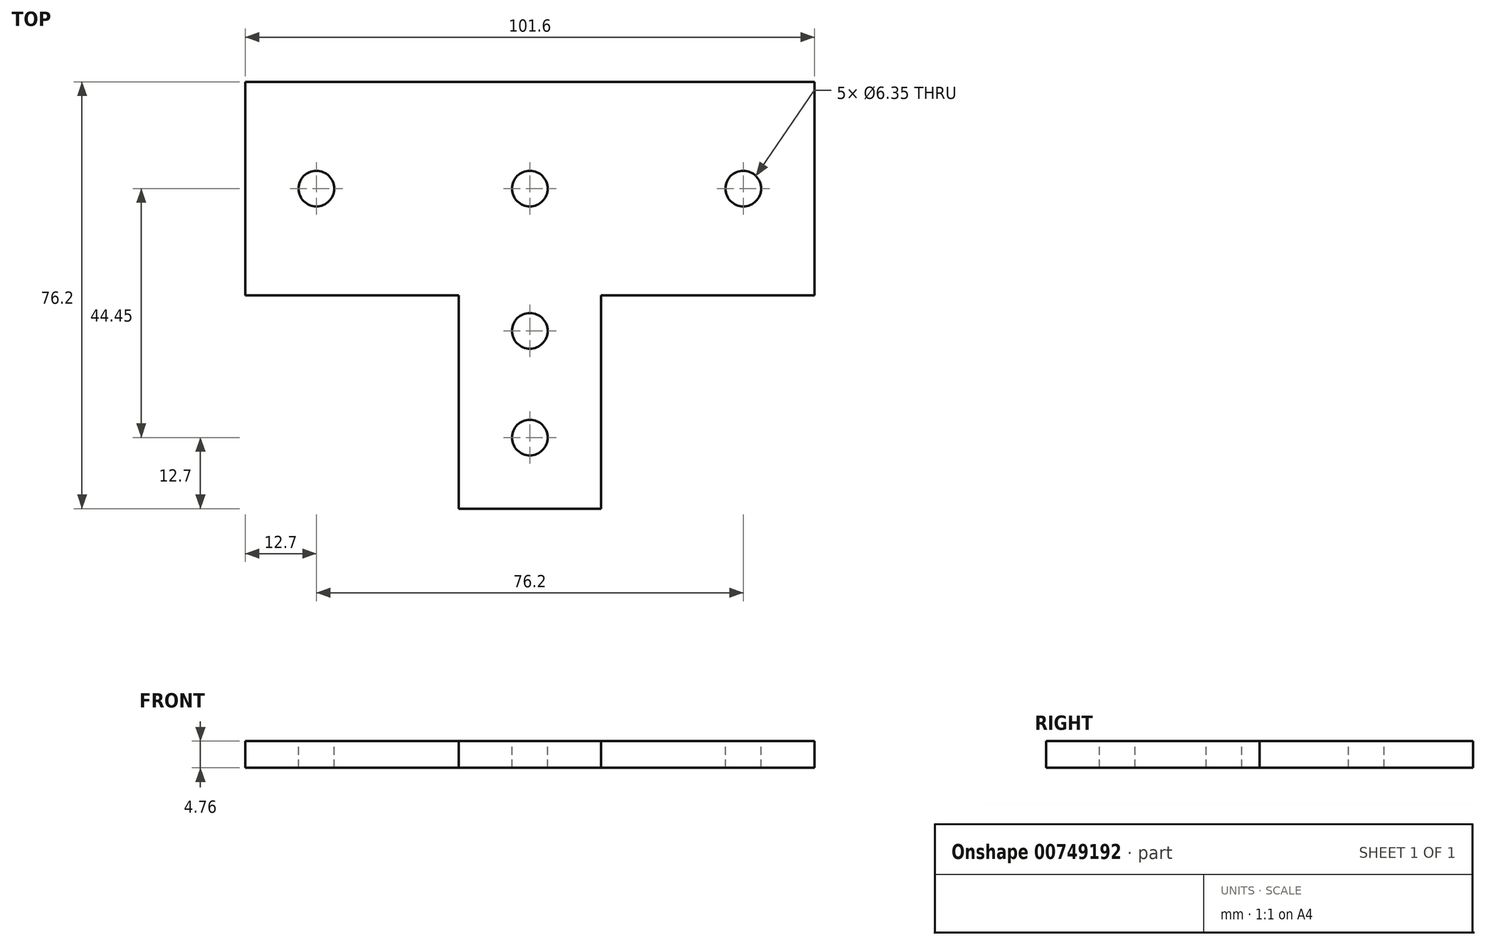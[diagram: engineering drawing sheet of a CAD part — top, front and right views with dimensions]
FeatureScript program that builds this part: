
annotation { "Feature Type Name" : "Feature", "Feature Type Description" : "" }
export const myFeature = defineFeature(function(context is Context, id is Id, definition is map)
    precondition{}
    {
        {
            var Q0;
            Q0=qCreatedBy(makeId("Top.planeOp"),FACE);
            var sketch = newSketch(context, id + "F0", { "sketchPlane" : qUnion([Q0])});
            skLineSegment(sketch, "E0.bottom", {"start": v(0, 0) * mm, "end": v(101.6, 0) * mm});
            skLineSegment(sketch, "E0.top", {"start": v(0, 76.2) * mm, "end": v(101.6, 76.2) * mm});
            skLineSegment(sketch, "E0.left", {"start": v(0, 0) * mm, "end": v(0, 76.2) * mm});
            skLineSegment(sketch, "E0.right", {"start": v(101.6, 0) * mm, "end": v(101.6, 76.2) * mm});
            skSolve(sketch);
        }
        {
            var Q0;
            Q0=qSketchRegion(id+"F0",true);
            extrude(context, id + "F1", {"entities" : qUnion([Q0]), "depth" : 4.76 * mm, "offsetDistance" : 25.4 * mm});
        }
        {
            var Q0;
            Q0=makeQuery(id+"F1.opExtrude","CAP_FACE",FACE,{"disambiguationData":[OSD([sQuery(id+"F0.wireOp",EDGE,"E0.bottom"),sQuery(id+"F0.wireOp",EDGE,"E0.top"),sQuery(id+"F0.wireOp",EDGE,"E0.left"),sQuery(id+"F0.wireOp",EDGE,"E0.right")])],"isStart":false});
            var sketch = newSketch(context, id + "F2", { "sketchPlane" : qUnion([Q0])});
            skLineSegment(sketch, "E1.bottom", {"start": v(101.6, 0) * mm, "end": v(63.5, 0) * mm});
            skLineSegment(sketch, "E1.top", {"start": v(101.6, 38.1) * mm, "end": v(63.5, 38.1) * mm});
            skLineSegment(sketch, "E1.left", {"start": v(101.6, 0) * mm, "end": v(101.6, 38.1) * mm});
            skLineSegment(sketch, "E1.right", {"start": v(63.5, 0) * mm, "end": v(63.5, 38.1) * mm});
            skLineSegment(sketch, "E2.bottom", {"start": v(0, 0) * mm, "end": v(38.1, 0) * mm});
            skLineSegment(sketch, "E2.top", {"start": v(0, 38.1) * mm, "end": v(38.1, 38.1) * mm});
            skLineSegment(sketch, "E2.left", {"start": v(0, 0) * mm, "end": v(0, 38.1) * mm});
            skLineSegment(sketch, "E2.right", {"start": v(38.1, 0) * mm, "end": v(38.1, 38.1) * mm});
            skSolve(sketch);
        }
        {
            var Q0;
            Q0=qSketchRegion(id+"F2",true);
            extrude(context, id + "F3", {"entities" : qUnion([Q0]), "operationType" : NewBodyOperationType.REMOVE, "oppositeDirection" : true, "depth" : 25.4 * mm, "offsetDistance" : 25.4 * mm});
        }
        {
            var Q0;
            Q0=makeQuery(id+"F1.opExtrude","CAP_FACE",FACE,{"disambiguationData":[OSD([sQuery(id+"F0.wireOp",EDGE,"E0.bottom"),sQuery(id+"F0.wireOp",EDGE,"E0.top"),sQuery(id+"F0.wireOp",EDGE,"E0.left"),sQuery(id+"F0.wireOp",EDGE,"E0.right")])],"isStart":false});
            var sketch = newSketch(context, id + "F4", { "sketchPlane" : qUnion([Q0])});
            skCircle(sketch, "E3", {"center": v(50.8, 12.7) * mm, "radius": 3.17 * mm});
            skCircle(sketch, "E4", {"center": v(50.8, 31.75) * mm, "radius": 3.17 * mm});
            skCircle(sketch, "E5", {"center": v(12.7, 57.15) * mm, "radius": 3.17 * mm});
            skCircle(sketch, "E6", {"center": v(50.8, 57.15) * mm, "radius": 3.17 * mm});
            skCircle(sketch, "E7", {"center": v(88.9, 57.15) * mm, "radius": 3.17 * mm});
            skSolve(sketch);
        }
        {
            var Q0;
            Q0=qSketchRegion(id+"F4",true);
            extrude(context, id + "F5", {"entities" : qUnion([Q0]), "operationType" : NewBodyOperationType.REMOVE, "oppositeDirection" : true, "depth" : 25.4 * mm, "offsetDistance" : 25.4 * mm});
        }
    });
